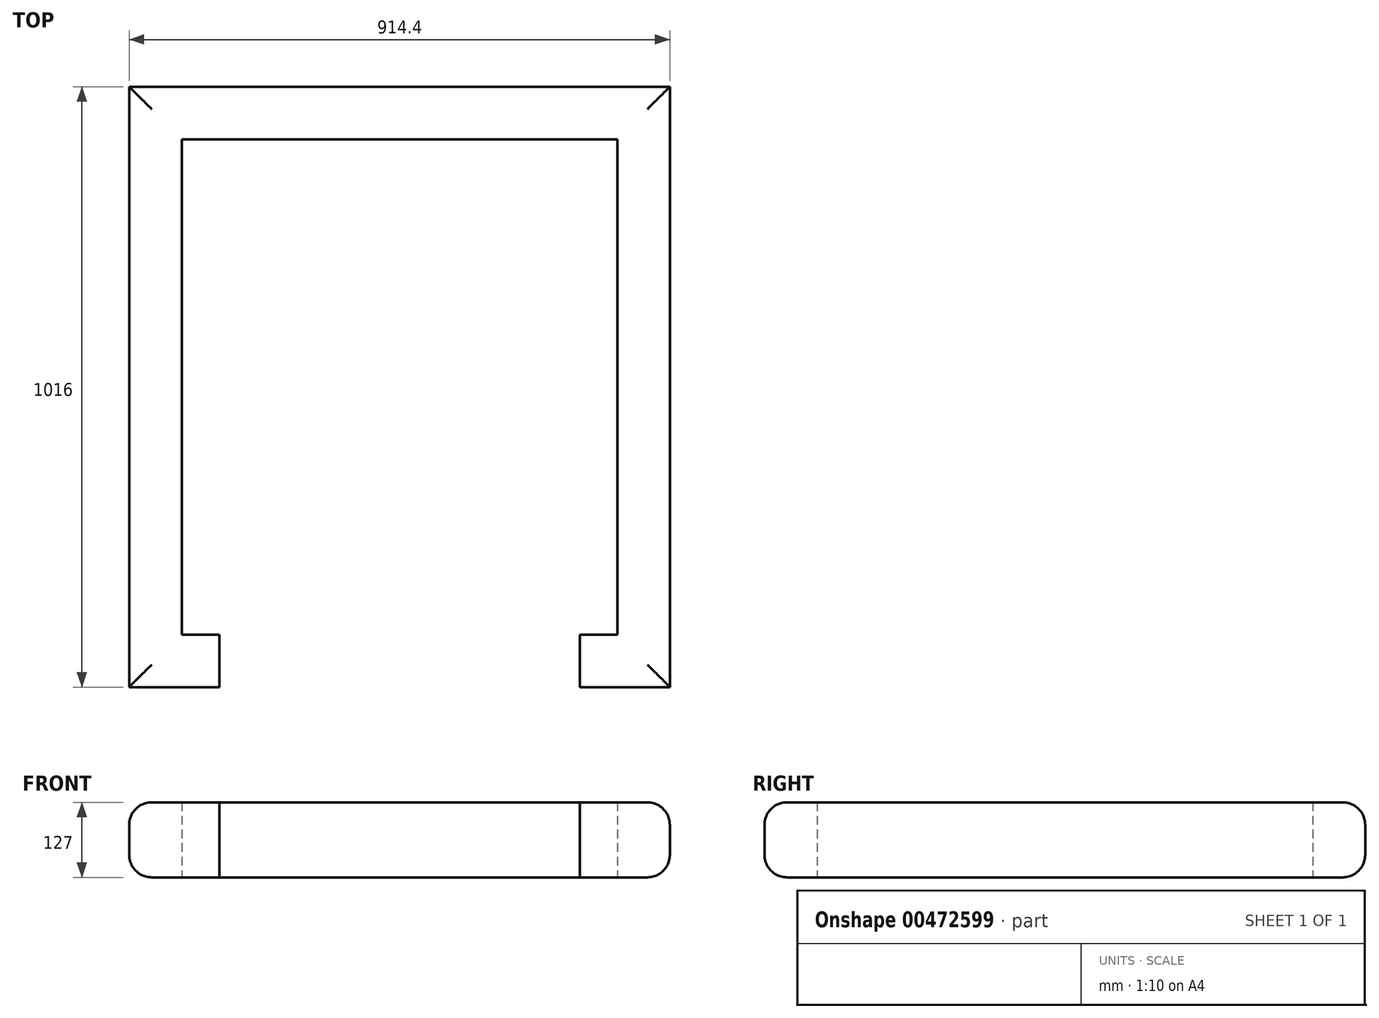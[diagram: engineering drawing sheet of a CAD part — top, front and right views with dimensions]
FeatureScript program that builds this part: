
annotation { "Feature Type Name" : "Feature", "Feature Type Description" : "" }
export const myFeature = defineFeature(function(context is Context, id is Id, definition is map)
    precondition{}
    {
        {
            var Q0;
            Q0=qCreatedBy(makeId("Top.planeOp"),FACE);
            var sketch = newSketch(context, id + "F0", { "sketchPlane" : qUnion([Q0])});
            skLineSegment(sketch, "E0.bottom", {"start": v(-444.08, 669.42) * mm, "end": v(470.32, 669.42) * mm});
            skLineSegment(sketch, "E0.top", {"start": v(-444.08, -346.58) * mm, "end": v(470.32, -346.58) * mm});
            skLineSegment(sketch, "E0.left", {"start": v(-444.08, 669.42) * mm, "end": v(-444.08, -346.58) * mm});
            skLineSegment(sketch, "E0.right", {"start": v(470.32, 669.42) * mm, "end": v(470.32, -346.58) * mm});
            skLineSegment(sketch, "E1.bottom", {"start": v(-355.18, 580.52) * mm, "end": v(381.42, 580.52) * mm});
            skLineSegment(sketch, "E1.top", {"start": v(-355.18, -257.68) * mm, "end": v(381.42, -257.68) * mm});
            skLineSegment(sketch, "E1.left", {"start": v(-355.18, 580.52) * mm, "end": v(-355.18, -257.68) * mm});
            skLineSegment(sketch, "E1.right", {"start": v(381.42, 580.52) * mm, "end": v(381.42, -257.68) * mm});
            skLineSegment(sketch, "E2.bottom", {"start": v(-291.68, -216.03) * mm, "end": v(317.92, -216.03) * mm});
            skLineSegment(sketch, "E2.top", {"start": v(-291.68, -422.33) * mm, "end": v(317.92, -422.33) * mm});
            skLineSegment(sketch, "E2.left", {"start": v(-291.68, -216.03) * mm, "end": v(-291.68, -422.33) * mm});
            skLineSegment(sketch, "E2.right", {"start": v(317.92, -216.03) * mm, "end": v(317.92, -422.33) * mm});
            skSolve(sketch);
        }
        {
            var Q0;
            Q0=makeQuery(id+"F0.imprint","IMPRINT",FACE,{"disambiguationData":[TD([[makeQuery(id+"F0.imprint","IMPRINT",EDGE,{"derivedFrom":sQuery(id+"F0.wireOp",EDGE,"E0.bottom")}),-1.0]])]});
            extrude(context, id + "F1", {"entities" : qUnion([Q0]), "depth" : 127 * mm});
        }
        {
            var Q0;
            Q0=makeQuery(id+"F1.opExtrude","CAP_EDGE",EDGE,{"disambiguationData":[OSD([sQuery(id+"F0.wireOp",EDGE,"E0.bottom")])],"isStart":true});
            var Q1;
            Q1=makeQuery(id+"F1.opExtrude","CAP_EDGE",EDGE,{"disambiguationData":[OSD([sQuery(id+"F0.wireOp",EDGE,"E0.bottom")])],"isStart":false});
            var Q2;
            Q2=makeQuery(id+"F1.opExtrude","CAP_EDGE",EDGE,{"disambiguationData":[OSD([sQuery(id+"F0.wireOp",EDGE,"E0.right")])],"isStart":false});
            var Q3;
            Q3=makeQuery(id+"F1.opExtrude","CAP_EDGE",EDGE,{"disambiguationData":[OSD([sQuery(id+"F0.wireOp",EDGE,"E0.right")])],"isStart":true});
            var Q4;
            Q4=makeQuery(id+"F1.opExtrude","CAP_EDGE",EDGE,{"disambiguationData":[OSD([sQuery(id+"F0.wireOp",EDGE,"E0.left")])],"isStart":true});
            var Q5;
            Q5=makeQuery(id+"F1.opExtrude","CAP_EDGE",EDGE,{"disambiguationData":[OSD([sQuery(id+"F0.wireOp",EDGE,"E0.left")])],"isStart":false});
            var Q6;
            {var subQ0=sQuery(id+"F0.wireOp",EDGE,"E0.top");Q6=makeQuery(id+"F1.opExtrude","CAP_EDGE",EDGE,{"disambiguationData":[OSD([subQ0]),TDD([makeQuery(id+"F0.imprint","IMPRINT",EDGE,{"disambiguationData":[TD([[makeQuery(id+"F0.imprint","INTERSECT",VERTEX,{"derivedFrom":[subQ0,sQuery(id+"F0.wireOp",EDGE,"E0.left")]}),-1.0]])],"derivedFrom":subQ0})])],"isStart":true});}
            var Q7;
            {var subQ0=sQuery(id+"F0.wireOp",EDGE,"E0.top");Q7=makeQuery(id+"F1.opExtrude","CAP_EDGE",EDGE,{"disambiguationData":[OSD([subQ0]),TDD([makeQuery(id+"F0.imprint","IMPRINT",EDGE,{"disambiguationData":[TD([[makeQuery(id+"F0.imprint","INTERSECT",VERTEX,{"derivedFrom":[subQ0,sQuery(id+"F0.wireOp",EDGE,"E0.left")]}),-1.0]])],"derivedFrom":subQ0})])],"isStart":false});}
            var Q8;
            {var subQ0=sQuery(id+"F0.wireOp",EDGE,"E0.top");Q8=makeQuery(id+"F1.opExtrude","CAP_EDGE",EDGE,{"disambiguationData":[OSD([subQ0]),TDD([makeQuery(id+"F0.imprint","IMPRINT",EDGE,{"disambiguationData":[TD([[makeQuery(id+"F0.imprint","INTERSECT",VERTEX,{"derivedFrom":[subQ0,sQuery(id+"F0.wireOp",EDGE,"E0.right")]}),1.0]])],"derivedFrom":subQ0})])],"isStart":false});}
            var Q9;
            {var subQ0=sQuery(id+"F0.wireOp",EDGE,"E0.top");Q9=makeQuery(id+"F1.opExtrude","CAP_EDGE",EDGE,{"disambiguationData":[OSD([subQ0]),TDD([makeQuery(id+"F0.imprint","IMPRINT",EDGE,{"disambiguationData":[TD([[makeQuery(id+"F0.imprint","INTERSECT",VERTEX,{"derivedFrom":[subQ0,sQuery(id+"F0.wireOp",EDGE,"E0.right")]}),1.0]])],"derivedFrom":subQ0})])],"isStart":true});}
            fillet(context, id + "F2", {"entities" : qUnion([Q0, Q1, Q2, Q3, Q4, Q5, Q6, Q7, Q8, Q9]), "tangentPropagation" : true, "radius" : 38.1 * mm, "defaultsChanged" : false, "vertexSettings" : [], "allowEdgeOverflow" : false});
        }
    });
